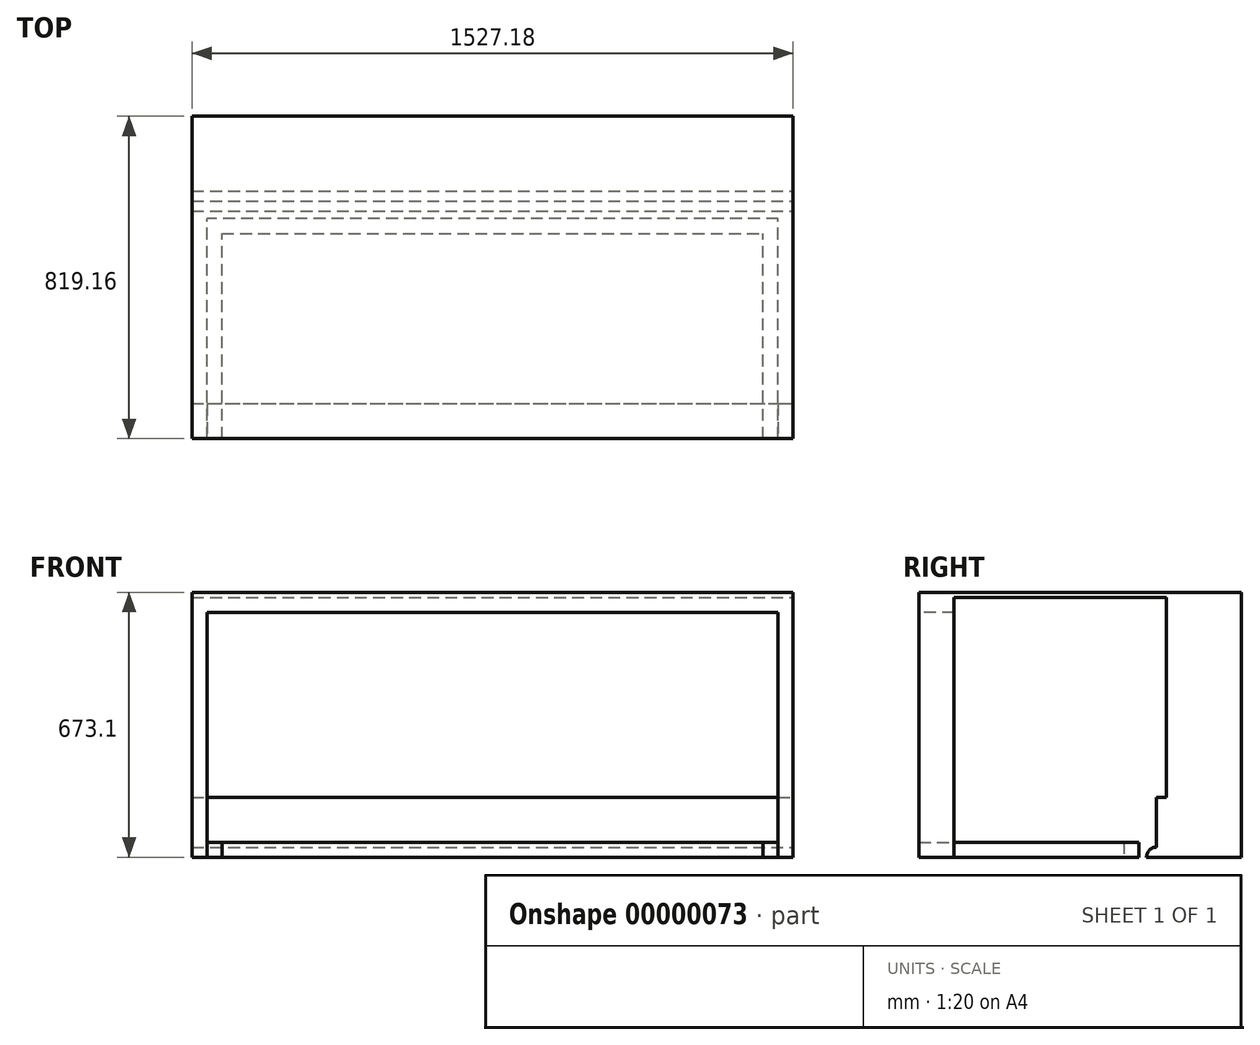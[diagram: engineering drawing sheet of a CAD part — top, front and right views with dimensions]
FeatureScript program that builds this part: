
annotation { "Feature Type Name" : "Feature", "Feature Type Description" : "" }
export const myFeature = defineFeature(function(context is Context, id is Id, definition is map)
    precondition{}
    {
        {
            var Q0;
            Q0=qCreatedBy(makeId("Top.planeOp"),FACE);
            var sketch = newSketch(context, id + "F0", { "sketchPlane" : qUnion([Q0])});
            skLineSegment(sketch, "E0.rect.bottom", {"start": v(-763.59, 409.58) * mm, "end": v(763.59, 409.58) * mm});
            skLineSegment(sketch, "E0.rect.top", {"start": v(-763.59, -409.57) * mm, "end": v(763.59, -409.57) * mm});
            skLineSegment(sketch, "E0.rect.left", {"start": v(-763.59, 409.58) * mm, "end": v(-763.59, -409.57) * mm});
            skLineSegment(sketch, "E0.rect.right", {"start": v(763.59, 409.58) * mm, "end": v(763.59, -409.57) * mm});
            skPoint(sketch, "E0.rect.middle", {"position": v(0, 0) * mm});
            skLineSegment(sketch, "E1", {"start": v(-763.59, -320.67) * mm, "end": v(763.59, -320.67) * mm});
            skLineSegment(sketch, "E2", {"start": v(725.49, -320.67) * mm, "end": v(725.49, -409.57) * mm});
            skLineSegment(sketch, "E3", {"start": v(0, 0) * mm, "end": v(0, 409.58) * mm, "construction": true});
            skLineSegment(sketch, "E4.0.MirrorCS", {"start": v(-725.49, -320.67) * mm, "end": v(-725.49, -409.57) * mm});
            skLineSegment(sketch, "E5", {"start": v(-763.59, 219.08) * mm, "end": v(763.59, 219.08) * mm});
            skSolve(sketch);
        }
        {
            var Q0;
            Q0 = qSketchRegion(id + "F0", true);
            extrude(context, id + "F1", {"entities" : qUnion([Q0]), "depth" : 12.7 * mm});
        }
        {
            var Q0;
            {var subQ0=sQuery(id+"F0.wireOp",EDGE,"E4.0.MirrorCS");Q0=makeQuery(id+"F0.imprint","IMPRINT",FACE,{"disambiguationData":[TD([[makeQuery(id+"F0.imprint","IMPRINT",EDGE,{"derivedFrom":subQ0}),-1.0]])]});}
            var Q1;
            {var subQ0=sQuery(id+"F0.wireOp",EDGE,"E2");Q1=makeQuery(id+"F0.imprint","IMPRINT",FACE,{"disambiguationData":[TD([[makeQuery(id+"F0.imprint","IMPRINT",EDGE,{"derivedFrom":subQ0}),1.0]])]});}
            var Q2;
            {var subQ2=sQuery(id+"F0.wireOp",EDGE,"E0.rect.bottom");Q2=makeQuery(id+"F0.imprint","IMPRINT",FACE,{"disambiguationData":[TD([[makeQuery(id+"F0.imprint","IMPRINT",EDGE,{"derivedFrom":subQ2}),-1.0]])]});}
            extrude(context, id + "F2", {"entities" : qUnion([Q0, Q1, Q2]), "operationType" : NewBodyOperationType.ADD, "oppositeDirection" : true, "depth" : 660.4 * mm});
        }
        {
            var Q0;
            {var subQ0=sQuery(id+"F0.wireOp",EDGE,"E0.rect.right");Q0=makeQuery(id+"F2.boolean.opBoolean","MERGE",FACE,{"derivedFrom":[makeQuery(id+"F1.opExtrude","SWEPT_FACE",FACE,{"disambiguationData":[OSD([subQ0])]}),makeQuery(id+"F2.opExtrude","SWEPT_FACE",FACE,{"disambiguationData":[OSD([subQ0]),TDD([makeQuery(id+"F0.imprint","IMPRINT",EDGE,{"disambiguationData":[TD([[makeQuery(id+"F0.imprint","INTERSECT",VERTEX,{"derivedFrom":[sQuery(id+"F0.wireOp",EDGE,"E0.rect.bottom"),subQ0]}),-1.0]])],"derivedFrom":subQ0})])]}),makeQuery(id+"F2.opExtrude","SWEPT_FACE",FACE,{"disambiguationData":[OSD([subQ0]),TDD([makeQuery(id+"F0.imprint","IMPRINT",EDGE,{"disambiguationData":[TD([[makeQuery(id+"F0.imprint","INTERSECT",VERTEX,{"derivedFrom":[sQuery(id+"F0.wireOp",EDGE,"E0.rect.top"),subQ0]}),1.0]])],"derivedFrom":subQ0})])]})]});}
            var sketch = newSketch(context, id + "F3", { "sketchPlane" : qUnion([Q0])});
            skLineSegment(sketch, "E6", {"start": v(168.28, -660.4) * mm, "end": v(219.08, -660.4) * mm});
            skLineSegment(sketch, "E7", {"start": v(219.08, -660.4) * mm, "end": v(219.08, -508) * mm});
            skLineSegment(sketch, "E8", {"start": v(219.08, -508) * mm, "end": v(193.68, -508) * mm});
            skLineSegment(sketch, "E9", {"start": v(193.68, -508) * mm, "end": v(193.68, -635) * mm});
            skArc(sketch, "E10", {"start": v(193.68, -635) * mm, "mid": v(175.71, -642.44) * mm, "end": v(168.28, -660.4) * mm});
            skLineSegment(sketch, "E11", {"start": v(193.68, -635) * mm, "end": v(168.28, -635) * mm, "construction": true});
            skLineSegment(sketch, "E12", {"start": v(168.28, -635) * mm, "end": v(168.28, -660.4) * mm, "construction": true});
            skSolve(sketch);
        }
        {
            var Q0;
            Q0 = qSketchRegion(id + "F3", true);
            var Q1;
            {var subQ0=sQuery(id+"F0.wireOp",EDGE,"E0.rect.left");Q1=makeQuery(id+"F2.boolean.opBoolean","MERGE",FACE,{"derivedFrom":[makeQuery(id+"F1.opExtrude","SWEPT_FACE",FACE,{"disambiguationData":[OSD([subQ0])]}),makeQuery(id+"F2.opExtrude","SWEPT_FACE",FACE,{"disambiguationData":[OSD([subQ0]),TDD([makeQuery(id+"F0.imprint","IMPRINT",EDGE,{"disambiguationData":[TD([[makeQuery(id+"F0.imprint","INTERSECT",VERTEX,{"derivedFrom":[sQuery(id+"F0.wireOp",EDGE,"E0.rect.bottom"),subQ0]}),-1.0]])],"derivedFrom":subQ0})])]}),makeQuery(id+"F2.opExtrude","SWEPT_FACE",FACE,{"disambiguationData":[OSD([subQ0]),TDD([makeQuery(id+"F0.imprint","IMPRINT",EDGE,{"disambiguationData":[TD([[makeQuery(id+"F0.imprint","INTERSECT",VERTEX,{"derivedFrom":[sQuery(id+"F0.wireOp",EDGE,"E0.rect.top"),subQ0]}),1.0]])],"derivedFrom":subQ0})])]})]});}
            extrude(context, id + "F4", {"entities" : qUnion([Q0]), "operationType" : NewBodyOperationType.ADD, "endBound" : BoundingType.UP_TO_SURFACE, "oppositeDirection" : true, "endBoundEntityFace" : qUnion([Q1]), "depth" : 25.4 * mm});
        }
        {
            var Q0;
            {var subQ1=sQuery(id+"F0.wireOp",EDGE,"E2");Q0=makeQuery(id+"F0.imprint","IMPRINT",FACE,{"disambiguationData":[TD([[makeQuery(id+"F0.imprint","IMPRINT",EDGE,{"derivedFrom":subQ1}),-1.0]])]});}
            extrude(context, id + "F5", {"entities" : qUnion([Q0]), "operationType" : NewBodyOperationType.ADD, "oppositeDirection" : true, "depth" : 38.1 * mm});
        }
        {
            var Q0;
            Q0=makeQuery(id+"F2.opExtrude","CAP_FACE",FACE,{"disambiguationData":[OSD([sQuery(id+"F0.wireOp",EDGE,"E0.rect.top"),sQuery(id+"F0.wireOp",EDGE,"E0.rect.left"),sQuery(id+"F0.wireOp",EDGE,"E1"),sQuery(id+"F0.wireOp",EDGE,"E4.0.MirrorCS")])],"isStart":false});
            var sketch = newSketch(context, id + "F6", { "sketchPlane" : qUnion([Q0])});
            skLineSegment(sketch, "E13.bottom", {"start": v(-725.49, 409.57) * mm, "end": v(-687.39, 409.57) * mm});
            skLineSegment(sketch, "E13.top", {"start": v(-725.49, -149.23) * mm, "end": v(-687.39, -149.23) * mm});
            skLineSegment(sketch, "E13.left", {"start": v(-725.49, 409.57) * mm, "end": v(-725.49, -149.23) * mm});
            skLineSegment(sketch, "E13.right", {"start": v(-687.39, 409.57) * mm, "end": v(-687.39, -149.23) * mm});
            skLineSegment(sketch, "E14", {"start": v(0, 0) * mm, "end": v(0, 408.34) * mm, "construction": true});
            skLineSegment(sketch, "E15.bottom", {"start": v(-687.39, -149.23) * mm, "end": v(687.39, -149.23) * mm});
            skLineSegment(sketch, "E15.top", {"start": v(-687.39, -111.13) * mm, "end": v(687.39, -111.13) * mm});
            skLineSegment(sketch, "E15.left", {"start": v(-687.39, -149.23) * mm, "end": v(-687.39, -111.13) * mm});
            skLineSegment(sketch, "E15.right", {"start": v(687.39, -149.23) * mm, "end": v(687.39, -111.13) * mm});
            skLineSegment(sketch, "E16.0.MirrorCS", {"start": v(725.49, -149.23) * mm, "end": v(687.39, -149.23) * mm});
            skLineSegment(sketch, "E16.1.MirrorCS", {"start": v(687.39, 409.57) * mm, "end": v(687.39, -149.23) * mm});
            skLineSegment(sketch, "E16.2.MirrorCS", {"start": v(725.49, 409.57) * mm, "end": v(725.49, -149.23) * mm});
            skLineSegment(sketch, "E16.3.MirrorCS", {"start": v(725.49, 409.57) * mm, "end": v(687.39, 409.57) * mm});
            skSolve(sketch);
        }
        {
            var Q0;
            Q0 = qSketchRegion(id + "F6", true);
            extrude(context, id + "F7", {"entities" : qUnion([Q0]), "oppositeDirection" : true, "depth" : 38.1 * mm});
        }
    });
